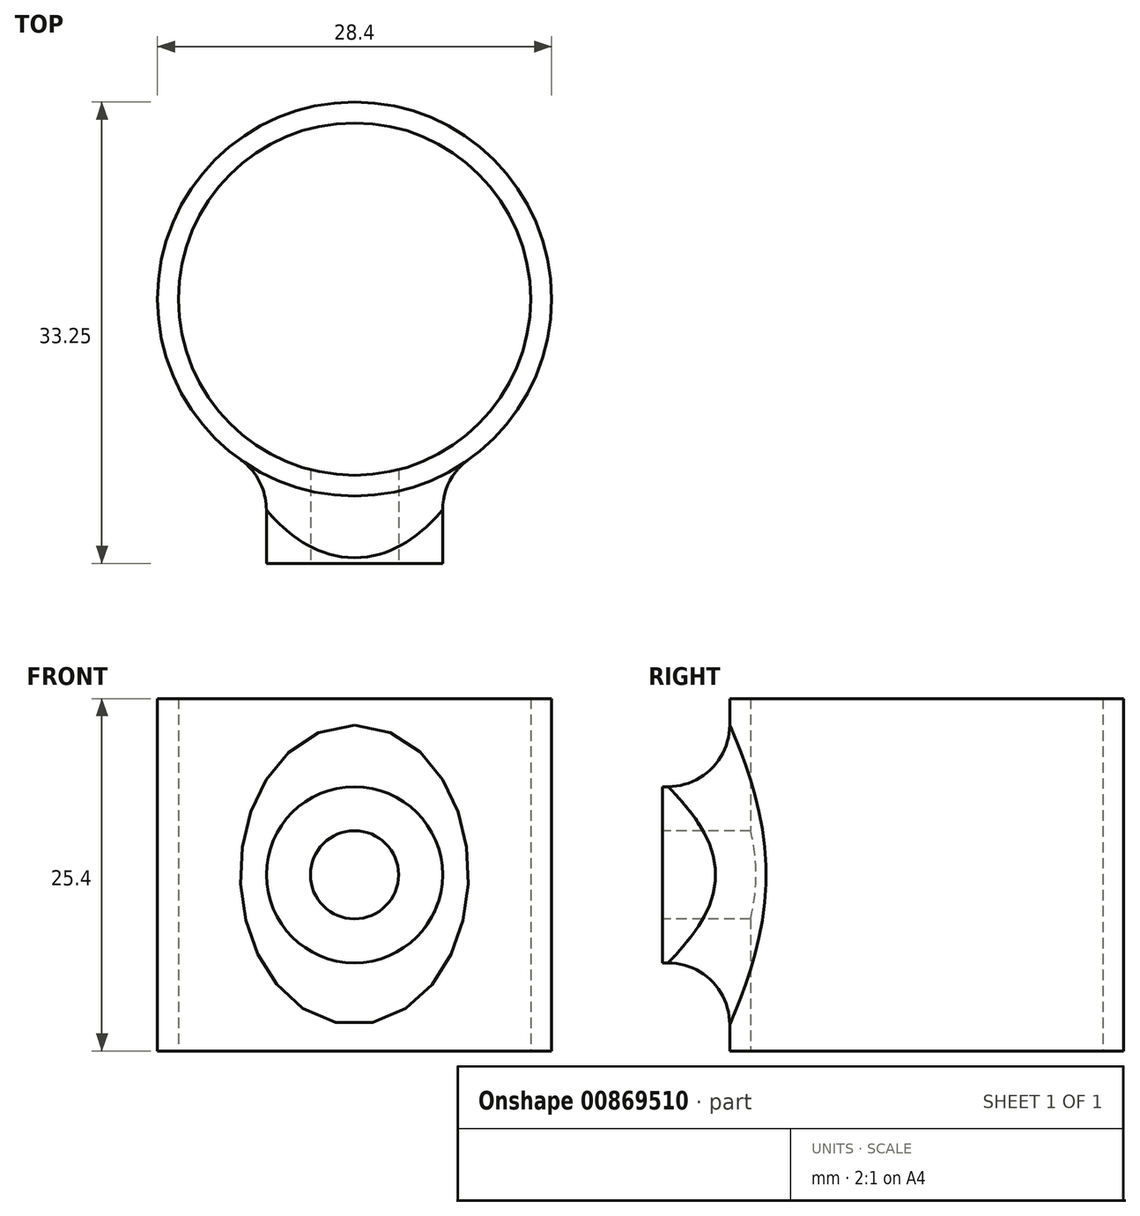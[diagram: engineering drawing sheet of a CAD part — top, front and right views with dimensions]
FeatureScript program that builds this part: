
annotation { "Feature Type Name" : "Feature", "Feature Type Description" : "" }
export const myFeature = defineFeature(function(context is Context, id is Id, definition is map)
    precondition{}
    {
        {
            var Q0;
            Q0=qCreatedBy(makeId("Top.planeOp"),FACE);
            var sketch = newSketch(context, id + "F0", { "sketchPlane" : qUnion([Q0])});
            skCircle(sketch, "E0", {"center": v(0, 0) * mm, "radius": 12.7 * mm, "construction": true});
            skCircle(sketch, "E1.0", {"center": v(0, 0) * mm, "radius": 14.2 * mm});
            skSolve(sketch);
        }
        {
            var Q0;
            Q0 = qSketchRegion(id + "F0", true);
            extrude(context, id + "F1", {"entities" : qUnion([Q0]), "depth" : 25.4 * mm, "offsetDistance" : 25.4 * mm});
        }
        {
            var Q0;
            Q0=qCreatedBy(makeId("Front.planeOp"),FACE);
            var sketch = newSketch(context, id + "F2", { "sketchPlane" : qUnion([Q0])});
            skCircle(sketch, "E2", {"center": v(0, 12.7) * mm, "radius": 6.35 * mm});
            skSolve(sketch);
        }
        {
            var Q0;
            Q0 = qSketchRegion(id + "F2", true);
            extrude(context, id + "F3", {"entities" : qUnion([Q0]), "operationType" : NewBodyOperationType.ADD, "depth" : 19.05 * mm, "offsetDistance" : 25.4 * mm});
        }
        {
            var Q0;
            Q0=sQuery(id+"F0.wireOp",VERTEX,"E0.center");
            var Q1;
            Q1=makeQuery(id+"F1.opExtrude","SWEPT_BODY",BODY,{"disambiguationData":[OSD([sQuery(id+"F0.wireOp",EDGE,"E1.0")])]});
            hole(context, id + "F4", {"style" : HoleStyle.SIMPLE, "endStyle" : HoleEndStyle.THROUGH, "oppositeDirection" : true, "holeDiameter" : 25.4 * mm, "majorDiameter" : 6.35 * mm, "isTappedThrough" : true, "tappedDepth" : 12.7 * mm, "tapClearance" : 3, "locations" : qUnion([Q0]), "scope" : qUnion([Q1])});
        }
        {
            var Q0;
            Q0=makeQuery(id+"F3.opExtrude","CAP_FACE",FACE,{"disambiguationData":[OSD([sQuery(id+"F2.wireOp",EDGE,"E2")])],"isStart":false});
            cPlane(context, id + "F5", {"entities" : qUnion([Q0]), "cplaneType" : CPlaneType.OFFSET, "offset" : 0 * mm, "width" : 152.4 * mm, "height" : 152.4 * mm});
        }
        {
            var Q0;
            Q0=qCreatedBy(id+"F5.planeOp",FACE);
            var sketch = newSketch(context, id + "F6", { "sketchPlane" : qUnion([Q0])});
            skPoint(sketch, "E3", {"position": v(0, 12.7) * mm});
            skSolve(sketch);
        }
        {
            var Q0;
            Q0=sQuery(id+"F6.wireOp",VERTEX,"E3");
            var Q1;
            Q1=makeQuery(id+"F1.opExtrude","SWEPT_BODY",BODY,{"disambiguationData":[OSD([sQuery(id+"F0.wireOp",EDGE,"E1.0")])]});
            hole(context, id + "F7", {"style" : HoleStyle.SIMPLE, "endStyle" : HoleEndStyle.BLIND, "holeDiameter" : 6.35 * mm, "majorDiameter" : 6.35 * mm, "holeDepth" : 19.05 * mm, "isTappedThrough" : true, "tappedDepth" : 12.7 * mm, "tapClearance" : 3, "locations" : qUnion([Q0]), "scope" : qUnion([Q1])});
        }
        {
            var Q0;
            Q0=makeQuery(id+"F3.boolean.opBoolean","INTERSECT",EDGE,{"derivedFrom":[makeQuery(id+"F1.opExtrude","SWEPT_FACE",FACE,{"disambiguationData":[OSD([sQuery(id+"F0.wireOp",EDGE,"E1.0")])]}),makeQuery(id+"F3.opExtrude","SWEPT_FACE",FACE,{"disambiguationData":[OSD([sQuery(id+"F2.wireOp",EDGE,"E2")])]})]});
            fillet(context, id + "F8", {"entities" : qUnion([Q0]), "radius" : 4.44 * mm, "tangentPropagation" : true, "allowEdgeOverflow" : false});
        }
    });
